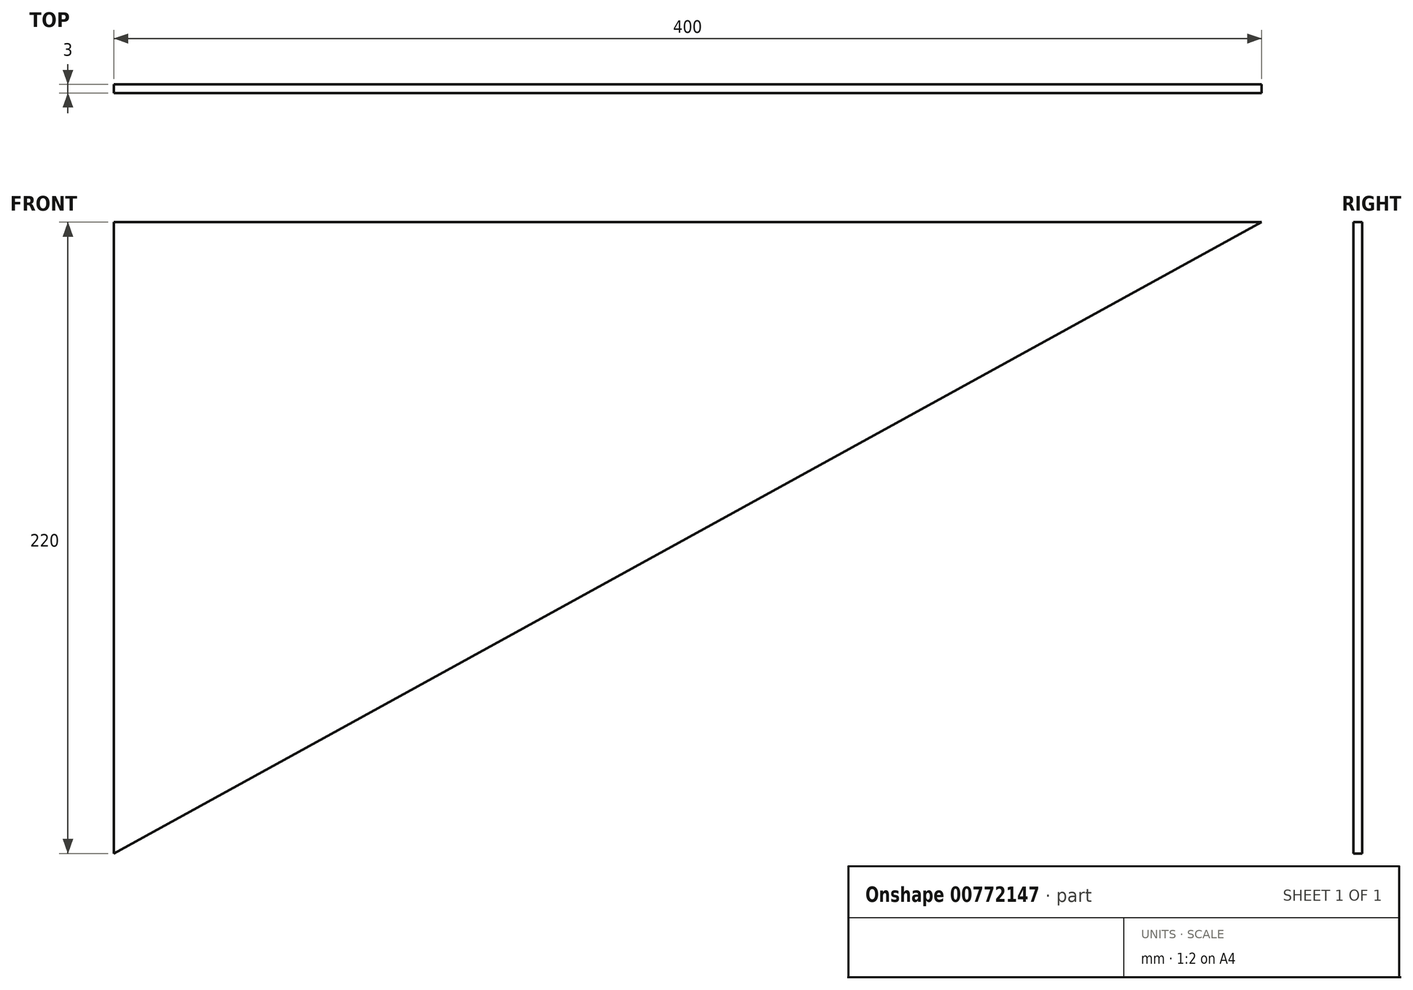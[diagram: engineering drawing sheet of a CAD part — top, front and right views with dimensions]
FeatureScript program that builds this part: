
annotation { "Feature Type Name" : "Feature", "Feature Type Description" : "" }
export const myFeature = defineFeature(function(context is Context, id is Id, definition is map)
    precondition{}
    {
        {
            var Q0;
            Q0=qCreatedBy(makeId("Front.planeOp"),FACE);
            var sketch = newSketch(context, id + "F0", { "sketchPlane" : qUnion([Q0])});
            skLineSegment(sketch, "E0.bottom", {"start": v(-184.88, 129.7) * mm, "end": v(215.12, 129.7) * mm});
            skLineSegment(sketch, "E0.top", {"start": v(-184.88, -90.3) * mm, "end": v(215.12, -90.3) * mm});
            skLineSegment(sketch, "E0.left", {"start": v(-184.88, 129.7) * mm, "end": v(-184.88, -90.3) * mm});
            skLineSegment(sketch, "E0.right", {"start": v(215.12, 129.7) * mm, "end": v(215.12, -90.3) * mm});
            skSolve(sketch);
        }
        {
            var Q0;
            Q0=makeQuery(id+"F0.imprint","IMPRINT",FACE,{"disambiguationData":[TD([[makeQuery(id+"F0.imprint","IMPRINT",EDGE,{"derivedFrom":sQuery(id+"F0.wireOp",EDGE,"E0.bottom")}),-1.0]])]});
            extrude(context, id + "F1", {"entities" : qUnion([Q0]), "depth" : 3 * mm, "offsetDistance" : 25.4 * mm});
        }
        {
            var Q0;
            Q0=makeQuery(id+"F1.opExtrude","CAP_FACE",FACE,{"disambiguationData":[OSD([sQuery(id+"F0.wireOp",EDGE,"E0.bottom"),sQuery(id+"F0.wireOp",EDGE,"E0.top"),sQuery(id+"F0.wireOp",EDGE,"E0.left"),sQuery(id+"F0.wireOp",EDGE,"E0.right")])],"isStart":false});
            var sketch = newSketch(context, id + "F2", { "sketchPlane" : qUnion([Q0])});
            skLineSegment(sketch, "E1.0.0", {"start": v(-184.88, 129.7) * mm, "end": v(-184.88, -90.3) * mm});
            skLineSegment(sketch, "E1.0.1", {"start": v(-184.88, -90.3) * mm, "end": v(215.12, -90.3) * mm});
            skLineSegment(sketch, "E1.0.2", {"start": v(215.12, -90.3) * mm, "end": v(215.12, 129.7) * mm});
            skLineSegment(sketch, "E1.0.3", {"start": v(215.12, 129.7) * mm, "end": v(-184.88, 129.7) * mm});
            skLineSegment(sketch, "E2", {"start": v(-184.88, 129.7) * mm, "end": v(215.12, -90.3) * mm});
            skLineSegment(sketch, "E3", {"start": v(215.12, 129.7) * mm, "end": v(-184.88, -90.3) * mm});
            skCircle(sketch, "E4", {"center": v(15.12, 19.7) * mm, "radius": 15 * mm});
            skSolve(sketch);
        }
        {
            var Q0;
            {var subQ0=sQuery(id+"F2.wireOp",EDGE,"E4");var subQ1=sQuery(id+"F2.wireOp",EDGE,"E2");var subQ2=makeQuery(id+"F2.imprint","INTERSECT",VERTEX,{"disambiguationData":[OD(0.0)],"derivedFrom":[subQ1,subQ0]});Q0=makeQuery(id+"F2.imprint","IMPRINT",FACE,{"disambiguationData":[TD([[makeQuery(id+"F2.imprint","IMPRINT",EDGE,{"disambiguationData":[TD([[subQ2,-1.0]])],"derivedFrom":subQ1}),1.0]])]});}
            var Q1;
            {var subQ0=sQuery(id+"F2.wireOp",EDGE,"E3");var subQ1=sQuery(id+"F2.wireOp",EDGE,"E2");var subQ2=makeQuery(id+"F2.imprint","INTERSECT",VERTEX,{"derivedFrom":[subQ1,subQ0]});Q1=makeQuery(id+"F2.imprint","IMPRINT",FACE,{"disambiguationData":[TD([[makeQuery(id+"F2.imprint","IMPRINT",EDGE,{"disambiguationData":[TD([[subQ2,-1.0]])],"derivedFrom":subQ1}),-1.0]])]});}
            var Q2;
            {var subQ0=sQuery(id+"F2.wireOp",EDGE,"E3");var subQ1=sQuery(id+"F2.wireOp",EDGE,"E2");var subQ2=makeQuery(id+"F2.imprint","INTERSECT",VERTEX,{"derivedFrom":[subQ1,subQ0]});Q2=makeQuery(id+"F2.imprint","IMPRINT",FACE,{"disambiguationData":[TD([[makeQuery(id+"F2.imprint","IMPRINT",EDGE,{"disambiguationData":[TD([[subQ2,-1.0]])],"derivedFrom":subQ1}),1.0]])]});}
            var Q3;
            {var subQ0=sQuery(id+"F2.wireOp",EDGE,"E4");var subQ1=sQuery(id+"F2.wireOp",EDGE,"E2");var subQ2=makeQuery(id+"F2.imprint","INTERSECT",VERTEX,{"disambiguationData":[OD(0.0)],"derivedFrom":[subQ1,subQ0]});Q3=makeQuery(id+"F2.imprint","IMPRINT",FACE,{"disambiguationData":[TD([[makeQuery(id+"F2.imprint","IMPRINT",EDGE,{"disambiguationData":[TD([[subQ2,-1.0]])],"derivedFrom":subQ1}),-1.0]])]});}
            extrude(context, id + "F3", {"entities" : qUnion([Q0, Q1, Q2, Q3]), "operationType" : NewBodyOperationType.REMOVE, "oppositeDirection" : true, "depth" : 35.56 * mm, "offsetDistance" : 25.4 * mm});
        }
    });
